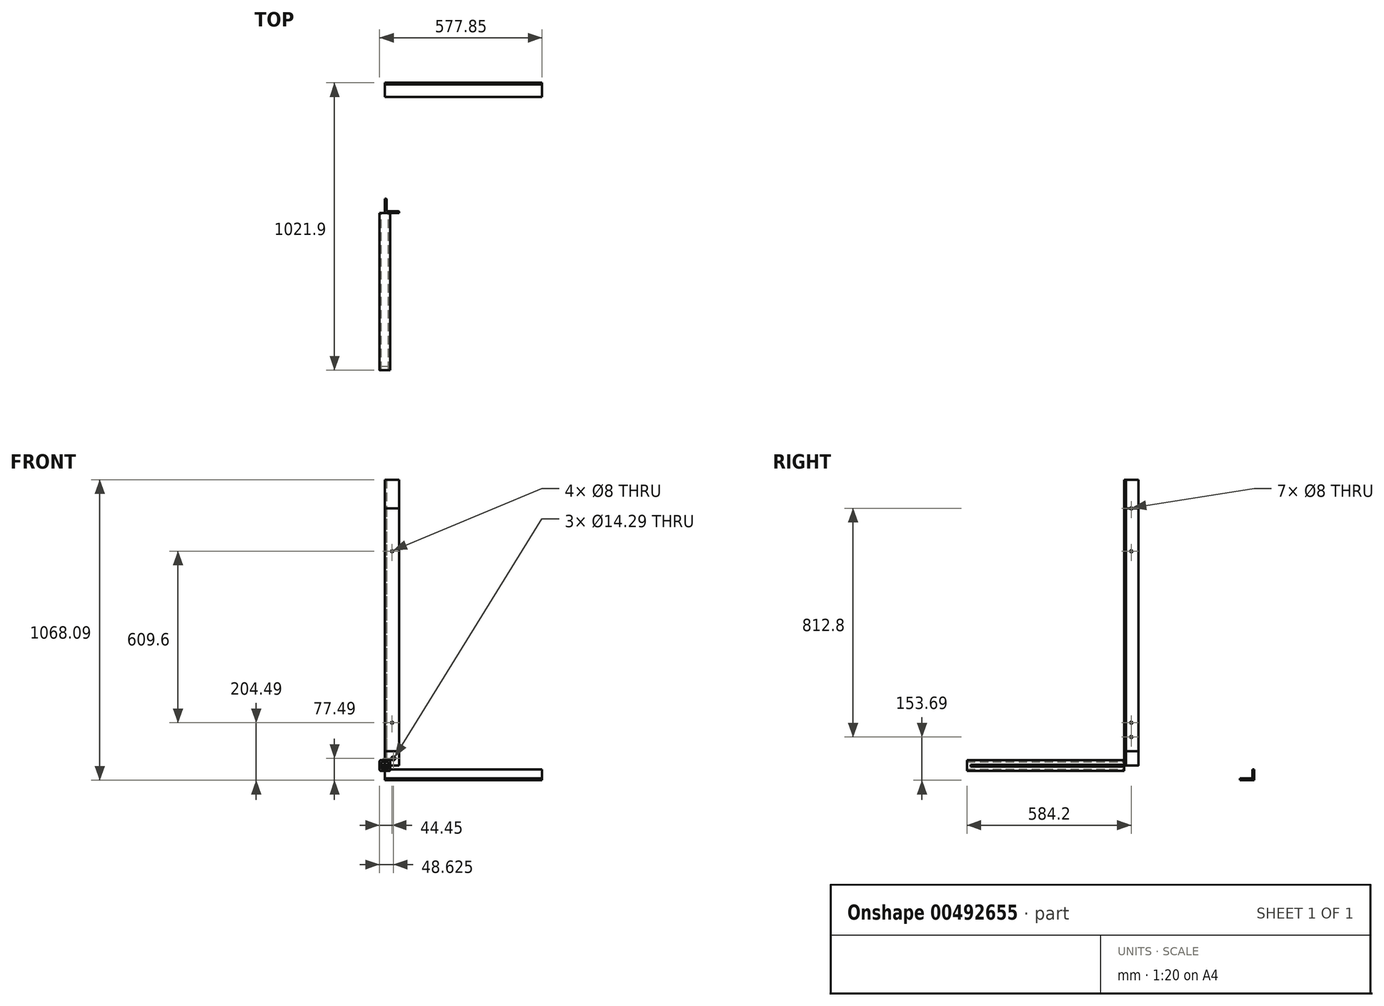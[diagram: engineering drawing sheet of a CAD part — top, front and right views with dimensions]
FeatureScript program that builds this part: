
annotation { "Feature Type Name" : "Feature", "Feature Type Description" : "" }
export const myFeature = defineFeature(function(context is Context, id is Id, definition is map)
    precondition{}
    {
        {
            assignVariable(context, id + "F0", {"name" : "h", "anyValue" : 914.4 * mm});
        }
        {
            assignVariable(context, id + "F1", {"name" : "L", "anyValue" : 1016 * mm});
        }
        {
            assignVariable(context, id + "F2", {"name" : "w", "anyValue" : 558.8 * mm});
        }
        {
            var Q0;
            Q0=qCreatedBy(makeId("Top.planeOp"),FACE);
            var sketch = newSketch(context, id + "F3", { "sketchPlane" : qUnion([Q0])});
            skLineSegment(sketch, "E0", {"start": v(0, 50.8) * mm, "end": v(0, 0) * mm});
            skLineSegment(sketch, "E1", {"start": v(0, 0) * mm, "end": v(50.8, 0) * mm});
            skLineSegment(sketch, "E2", {"start": v(50.8, 0) * mm, "end": v(50.8, 3.35) * mm});
            skLineSegment(sketch, "E3", {"start": v(47.8, 6.35) * mm, "end": v(11.35, 6.35) * mm});
            skLineSegment(sketch, "E4", {"start": v(6.35, 11.35) * mm, "end": v(6.35, 47.8) * mm});
            skLineSegment(sketch, "E5", {"start": v(3.35, 50.8) * mm, "end": v(0, 50.8) * mm});
            skPoint(sketch, "E6.visualSharp", {"position": v(6.35, 6.35) * mm});
            skArc(sketch, "E6.filletArc", {"start": v(6.35, 11.35) * mm, "mid": v(7.81, 7.81) * mm, "end": v(11.35, 6.35) * mm});
            skPoint(sketch, "E7.visualSharp", {"position": v(6.35, 50.8) * mm});
            skArc(sketch, "E7.filletArc", {"start": v(6.35, 47.8) * mm, "mid": v(5.47, 49.92) * mm, "end": v(3.35, 50.8) * mm});
            skPoint(sketch, "E8.visualSharp", {"position": v(50.8, 6.35) * mm});
            skArc(sketch, "E8.filletArc", {"start": v(50.8, 3.35) * mm, "mid": v(49.92, 5.47) * mm, "end": v(47.8, 6.35) * mm});
            skSolve(sketch);
        }
        {
            var Q0;
            Q0 = qSketchRegion(id + "F3", true);
            extrude(context, id + "F4", {"entities" : qUnion([Q0]), "depth" : getVariable(context, 'h'), "offsetDistance" : 25 * mm});
        }
        {
            var Q0;
            Q0 = qSketchRegion(id + "F3", true);
            extrude(context, id + "F5", {"entities" : qUnion([Q0]), "depth" : getVariable(context, 'L'), "offsetDistance" : 25 * mm});
        }
        {
            var Q0;
            Q0 = qSketchRegion(id + "F3", true);
            extrude(context, id + "F6", {"entities" : qUnion([Q0]), "depth" : getVariable(context, 'w'), "offsetDistance" : 25 * mm});
        }
        {
            var Q0;
            Q0 = qSketchRegion(id + "F3", true);
            extrude(context, id + "F7", {"entities" : qUnion([Q0]), "depth" : 50.8 * mm, "offsetDistance" : 25 * mm});
        }
        {
            var Q0;
            Q0=makeQuery(id+"F7.opExtrude","SWEPT_FACE",FACE,{"disambiguationData":[OSD([sQuery(id+"F3.wireOp",EDGE,"E3")])]});
            var sketch = newSketch(context, id + "F8", { "sketchPlane" : qUnion([Q0])});
            skLineSegment(sketch, "E9", {"start": v(-29.57, 0) * mm, "end": v(-29.58, 50.8) * mm, "construction": true});
            skLineSegment(sketch, "E10", {"start": v(-47.8, 25.4) * mm, "end": v(-11.35, 25.4) * mm, "construction": true});
            skCircle(sketch, "E11", {"center": v(-29.57, 25.4) * mm, "radius": 7.14 * mm});
            skSolve(sketch);
        }
        {
            var Q0;
            Q0=makeQuery(id+"F8.imprint","IMPRINT",FACE,{"disambiguationData":[TD([[makeQuery(id+"F8.imprint","IMPRINT",EDGE,{"derivedFrom":sQuery(id+"F8.wireOp",EDGE,"E11")}),1.0]])]});
            extrude(context, id + "F9", {"entities" : qUnion([Q0]), "operationType" : NewBodyOperationType.REMOVE, "endBound" : BoundingType.THROUGH_ALL, "oppositeDirection" : true, "depth" : 25 * mm, "offsetDistance" : 25 * mm});
        }
        {
            var Q0;
            Q0=makeQuery(id+"F4.opExtrude","SWEPT_FACE",FACE,{"disambiguationData":[OSD([sQuery(id+"F3.wireOp",EDGE,"E1")])]});
            var sketch = newSketch(context, id + "F10", { "sketchPlane" : qUnion([Q0])});
            skLineSegment(sketch, "E12", {"start": v(25.4, 914.4) * mm, "end": v(25.4, 0) * mm, "construction": true});
            skCircle(sketch, "E13", {"center": v(25.4, 762) * mm, "radius": 4 * mm});
            skCircle(sketch, "E14", {"center": v(25.4, 152.4) * mm, "radius": 4 * mm});
            skSolve(sketch);
        }
        {
            var Q0;
            Q0 = qSketchRegion(id + "F10", true);
            extrude(context, id + "F11", {"entities" : qUnion([Q0]), "operationType" : NewBodyOperationType.REMOVE, "endBound" : BoundingType.THROUGH_ALL, "oppositeDirection" : true, "depth" : 25 * mm, "offsetDistance" : 25 * mm});
        }
        {
            var Q0;
            Q0=makeQuery(id+"F4.opExtrude","SWEPT_FACE",FACE,{"disambiguationData":[OSD([sQuery(id+"F3.wireOp",EDGE,"E0")])]});
            var sketch = newSketch(context, id + "F12", { "sketchPlane" : qUnion([Q0])});
            skLineSegment(sketch, "E15", {"start": v(-25.4, 914.4) * mm, "end": v(-25.4, 0) * mm, "construction": true});
            skCircle(sketch, "E16", {"center": v(-25.4, 762) * mm, "radius": 4 * mm});
            skCircle(sketch, "E17", {"center": v(-25.4, 152.4) * mm, "radius": 4 * mm});
            skSolve(sketch);
        }
        {
            var Q0;
            Q0 = qSketchRegion(id + "F12", true);
            extrude(context, id + "F13", {"entities" : qUnion([Q0]), "operationType" : NewBodyOperationType.REMOVE, "endBound" : BoundingType.THROUGH_ALL, "oppositeDirection" : true, "depth" : 25 * mm, "offsetDistance" : 25 * mm});
        }
        {
            var Q0;
            Q0=makeQuery(id+"F5.opExtrude","SWEPT_FACE",FACE,{"disambiguationData":[OSD([sQuery(id+"F3.wireOp",EDGE,"E0")])]});
            var sketch = newSketch(context, id + "F14", { "sketchPlane" : qUnion([Q0])});
            skCircle(sketch, "E18", {"center": v(-25.4, 914.4) * mm, "radius": 4 * mm});
            skLineSegment(sketch, "E19", {"start": v(-50.8, 508) * mm, "end": v(0, 508) * mm, "construction": true});
            skLineSegment(sketch, "E20", {"start": v(-25.4, 0) * mm, "end": v(-25.4, 1016) * mm, "construction": true});
            skCircle(sketch, "E21.MirrorC", {"center": v(-25.4, 101.6) * mm, "radius": 4 * mm});
            skSolve(sketch);
        }
        {
            var Q0;
            Q0 = qSketchRegion(id + "F14", true);
            extrude(context, id + "F15", {"entities" : qUnion([Q0]), "operationType" : NewBodyOperationType.REMOVE, "endBound" : BoundingType.THROUGH_ALL, "oppositeDirection" : true, "depth" : 25 * mm, "offsetDistance" : 25 * mm});
        }
        {
            var Q0;
            Q0=qCreatedBy(makeId("Front.planeOp"),FACE);
            var sketch = newSketch(context, id + "F16", { "sketchPlane" : qUnion([Q0])});
            skLineSegment(sketch, "E22.bottom", {"start": v(19.05, -3.17) * mm, "end": v(-19.05, -3.18) * mm});
            skLineSegment(sketch, "E22.top", {"start": v(19.05, 3.18) * mm, "end": v(-19.05, 3.17) * mm});
            skLineSegment(sketch, "E22.left", {"start": v(19.05, -3.17) * mm, "end": v(19.05, 3.18) * mm});
            skLineSegment(sketch, "E22.right", {"start": v(-19.05, -3.18) * mm, "end": v(-19.05, 3.18) * mm});
            skPoint(sketch, "E22.middle", {"position": v(0, 0) * mm});
            skSolve(sketch);
        }
        {
            var Q0;
            Q0 = qSketchRegion(id + "F16", true);
            extrude(context, id + "F17", {"entities" : qUnion([Q0]), "depth" : getVariable(context, 'w') - 12.7 * mm, "offsetDistance" : 25 * mm});
        }
        {
            var Q0;
            Q0=qCreatedBy(makeId("Front.planeOp"),FACE);
            var sketch = newSketch(context, id + "F18", { "sketchPlane" : qUnion([Q0])});
            skLineSegment(sketch, "E23.bottom", {"start": v(15.05, -19.05) * mm, "end": v(-15.05, -19.05) * mm});
            skLineSegment(sketch, "E23.top", {"start": v(15.05, 19.05) * mm, "end": v(-15.05, 19.05) * mm});
            skLineSegment(sketch, "E23.left", {"start": v(19.05, -15.05) * mm, "end": v(19.05, 15.05) * mm});
            skLineSegment(sketch, "E23.right", {"start": v(-19.05, -15.05) * mm, "end": v(-19.05, 15.05) * mm});
            skPoint(sketch, "E23.middle", {"position": v(0, 0) * mm});
            skLineSegment(sketch, "E24.bottom", {"start": v(12.7, -12.7) * mm, "end": v(-12.7, -12.7) * mm});
            skLineSegment(sketch, "E24.top", {"start": v(12.7, 12.7) * mm, "end": v(-12.7, 12.7) * mm});
            skLineSegment(sketch, "E24.left", {"start": v(12.7, -12.7) * mm, "end": v(12.7, 12.7) * mm});
            skLineSegment(sketch, "E24.right", {"start": v(-12.7, -12.7) * mm, "end": v(-12.7, 12.7) * mm});
            skPoint(sketch, "E25.visualSharp", {"position": v(-19.05, 19.05) * mm});
            skArc(sketch, "E25.filletArc", {"start": v(-15.05, 19.05) * mm, "mid": v(-17.88, 17.88) * mm, "end": v(-19.05, 15.05) * mm});
            skPoint(sketch, "E26.visualSharp", {"position": v(19.05, 19.05) * mm});
            skArc(sketch, "E26.filletArc", {"start": v(19.05, 15.05) * mm, "mid": v(17.88, 17.88) * mm, "end": v(15.05, 19.05) * mm});
            skPoint(sketch, "E27.visualSharp", {"position": v(19.05, -19.05) * mm});
            skArc(sketch, "E27.filletArc", {"start": v(15.05, -19.05) * mm, "mid": v(17.88, -17.88) * mm, "end": v(19.05, -15.05) * mm});
            skPoint(sketch, "E28.visualSharp", {"position": v(-19.05, -19.05) * mm});
            skArc(sketch, "E28.filletArc", {"start": v(-19.05, -15.05) * mm, "mid": v(-17.88, -17.88) * mm, "end": v(-15.05, -19.05) * mm});
            skSolve(sketch);
        }
        {
            var Q0;
            Q0 = qSketchRegion(id + "F18", true);
            extrude(context, id + "F19", {"entities" : qUnion([Q0]), "depth" : getVariable(context, 'w'), "offsetDistance" : 25 * mm});
        }
        {
            var Q0;
            Q0=qCreatedBy(makeId("Right.planeOp"),FACE);
            var sketch = newSketch(context, id + "F20", { "sketchPlane" : qUnion([Q0])});
            skLineSegment(sketch, "E29", {"start": v(463.1, -14) * mm, "end": v(463.1, -52.1) * mm});
            skLineSegment(sketch, "E30", {"start": v(463.1, -52.1) * mm, "end": v(412.3, -52.1) * mm});
            skLineSegment(sketch, "E31", {"start": v(412.3, -52.1) * mm, "end": v(412.3, -45.74) * mm});
            skLineSegment(sketch, "E32", {"start": v(412.3, -45.74) * mm, "end": v(451.75, -45.74) * mm});
            skLineSegment(sketch, "E33", {"start": v(456.75, -40.74) * mm, "end": v(456.75, -14) * mm});
            skLineSegment(sketch, "E34", {"start": v(456.75, -14) * mm, "end": v(463.1, -14) * mm});
            skPoint(sketch, "E35.visualSharp", {"position": v(456.75, -45.74) * mm});
            skArc(sketch, "E35.filletArc", {"start": v(451.75, -45.74) * mm, "mid": v(455.3, -44.28) * mm, "end": v(456.75, -40.74) * mm});
            skSolve(sketch);
        }
        {
            var Q0;
            Q0 = qSketchRegion(id + "F20", true);
            extrude(context, id + "F21", {"entities" : qUnion([Q0]), "depth" : (getVariable(context, 'w')), "offsetDistance" : 25 * mm});
        }
        {
            var Q0;
            Q0=makeQuery(id+"F6.opExtrude","SWEPT_BODY",BODY,{"disambiguationData":[OSD([sQuery(id+"F3.wireOp",EDGE,"E0"),sQuery(id+"F3.wireOp",EDGE,"E1"),sQuery(id+"F3.wireOp",EDGE,"E2"),sQuery(id+"F3.wireOp",EDGE,"E3"),sQuery(id+"F3.wireOp",EDGE,"E4"),sQuery(id+"F3.wireOp",EDGE,"E5"),sQuery(id+"F3.wireOp",EDGE,"E6.filletArc"),sQuery(id+"F3.wireOp",EDGE,"E7.filletArc"),sQuery(id+"F3.wireOp",EDGE,"E8.filletArc")])]});
            deleteBodies(context, id + "F22", {"entities" : qUnion([Q0])});
        }
    });
